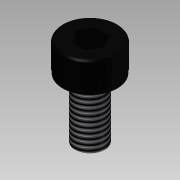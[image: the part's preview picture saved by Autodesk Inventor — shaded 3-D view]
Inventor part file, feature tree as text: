
AUTODESK INVENTOR PART (.ipt)
format: ipt  version: 2014 (Build 180170000, 170)  size: 119,296 bytes
history: native  units: mm
features: extrude x4, sketch x4, fillet x1, thread x1, reference x1
ambient origin geometry x8: Origin, YZ Plane, XZ Plane, XY Plane, X Axis, Y Axis, Z Axis, Center Point
bodies: Solid1 (feature_tree)
feature tree (11):
  extrude  "Extrusion1"  Depth=6.0mm TaperAngle=0.0deg
  extrude  "Extrusion2"  Depth=3.0mm TaperAngle=0.0deg
  fillet  "Fillet1"  Radius=0.3mm
  extrude  "Extrusion3"  Depth=0.5mm TaperAngle=0.0deg
  extrude  "Extrusion4"  Depth=2.0mm TaperAngle=0.0deg
  thread  "Thread1"  [1 undecoded]
  sketch  "Sketch1"  dims[d0=3.0mm d1=6.0mm d2=0.0mm]
  reference  "Reference1"
  sketch  "Sketch2"  dims[d3=5.6mm d4=3.0mm d5=0.0mm d6=0.3mm]
  sketch  "Sketch3"  dims[d7=5.5mm d8=0.5mm d9=0.0mm]
  sketch  "Sketch4"  dims[d10=2.5mm d11=2.0mm d12=0.0mm d13=10.0mm d14=0.0mm]
note: 1 required parameter value undecoded (feature->parameter linkage not recoverable at this tier; creation-order binding heuristic only, values carry confidence <= 0.55)
